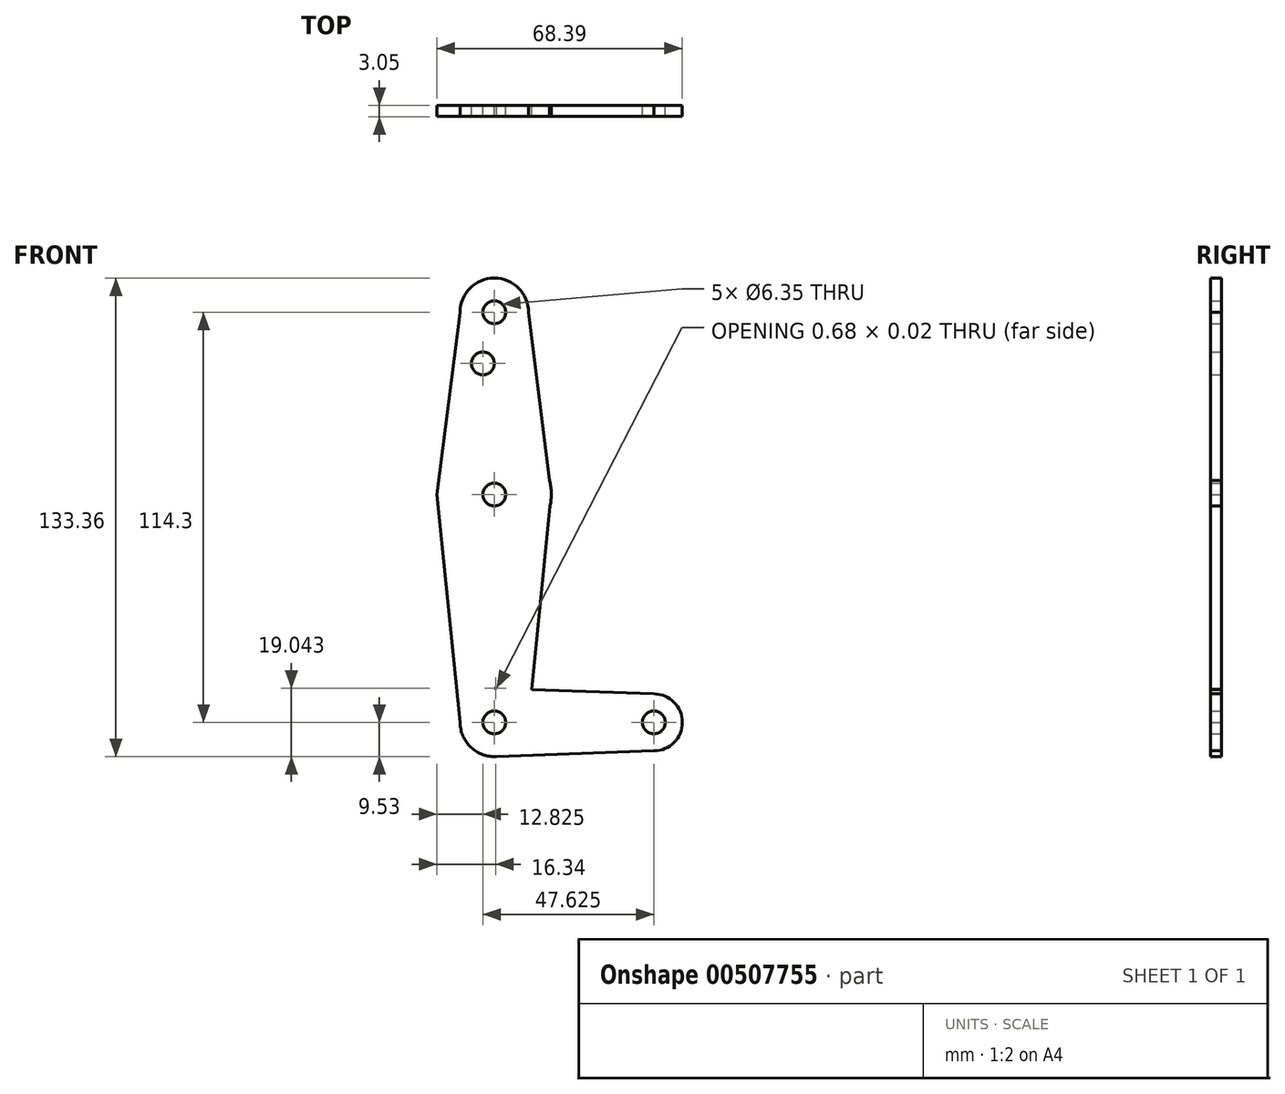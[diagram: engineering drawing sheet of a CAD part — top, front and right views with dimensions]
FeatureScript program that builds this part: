
annotation { "Feature Type Name" : "Feature", "Feature Type Description" : "" }
export const myFeature = defineFeature(function(context is Context, id is Id, definition is map)
    precondition{}
    {
        {
            var Q0;
            Q0=qCreatedBy(makeId("Front.planeOp"),FACE);
            var sketch = newSketch(context, id + "F0", { "sketchPlane" : qUnion([Q0])});
            skCircle(sketch, "E0", {"center": v(0, 114.3) * mm, "radius": 9.53 * mm});
            skCircle(sketch, "E1", {"center": v(0, 63.5) * mm, "radius": 15.88 * mm});
            skCircle(sketch, "E2", {"center": v(0, 0) * mm, "radius": 9.53 * mm});
            skCircle(sketch, "E3", {"center": v(44.45, 0) * mm, "radius": 7.94 * mm});
            skLineSegment(sketch, "E4", {"start": v(9.52, 114.3) * mm, "end": v(15.87, 63.5) * mm});
            skLineSegment(sketch, "E5", {"start": v(15.87, 63.5) * mm, "end": v(9.53, 0) * mm});
            skCircle(sketch, "E6", {"center": v(0, 114.3) * mm, "radius": 3.18 * mm});
            skCircle(sketch, "E7", {"center": v(0, 63.5) * mm, "radius": 3.18 * mm});
            skCircle(sketch, "E8", {"center": v(0, 0) * mm, "radius": 3.18 * mm});
            skCircle(sketch, "E9", {"center": v(44.45, 0) * mm, "radius": 3.18 * mm});
            skCircle(sketch, "E10", {"center": v(-3.18, 100.03) * mm, "radius": 3.18 * mm});
            skLineSegment(sketch, "E11", {"start": v(-9.53, 114.3) * mm, "end": v(-16, 63.5) * mm});
            skLineSegment(sketch, "E12", {"start": v(-16, 63.5) * mm, "end": v(-9.52, 0) * mm});
            skLineSegment(sketch, "E13", {"start": v(0, 9.53) * mm, "end": v(44.45, 7.94) * mm});
            skLineSegment(sketch, "E14", {"start": v(0, -9.53) * mm, "end": v(44.45, -7.94) * mm});
            skSolve(sketch);
        }
        {
            var Q0;
            Q0 = qSketchRegion(id + "F0", true);
            extrude(context, id + "F1", {"entities" : qUnion([Q0]), "depth" : 3.05 * mm});
        }
    });
